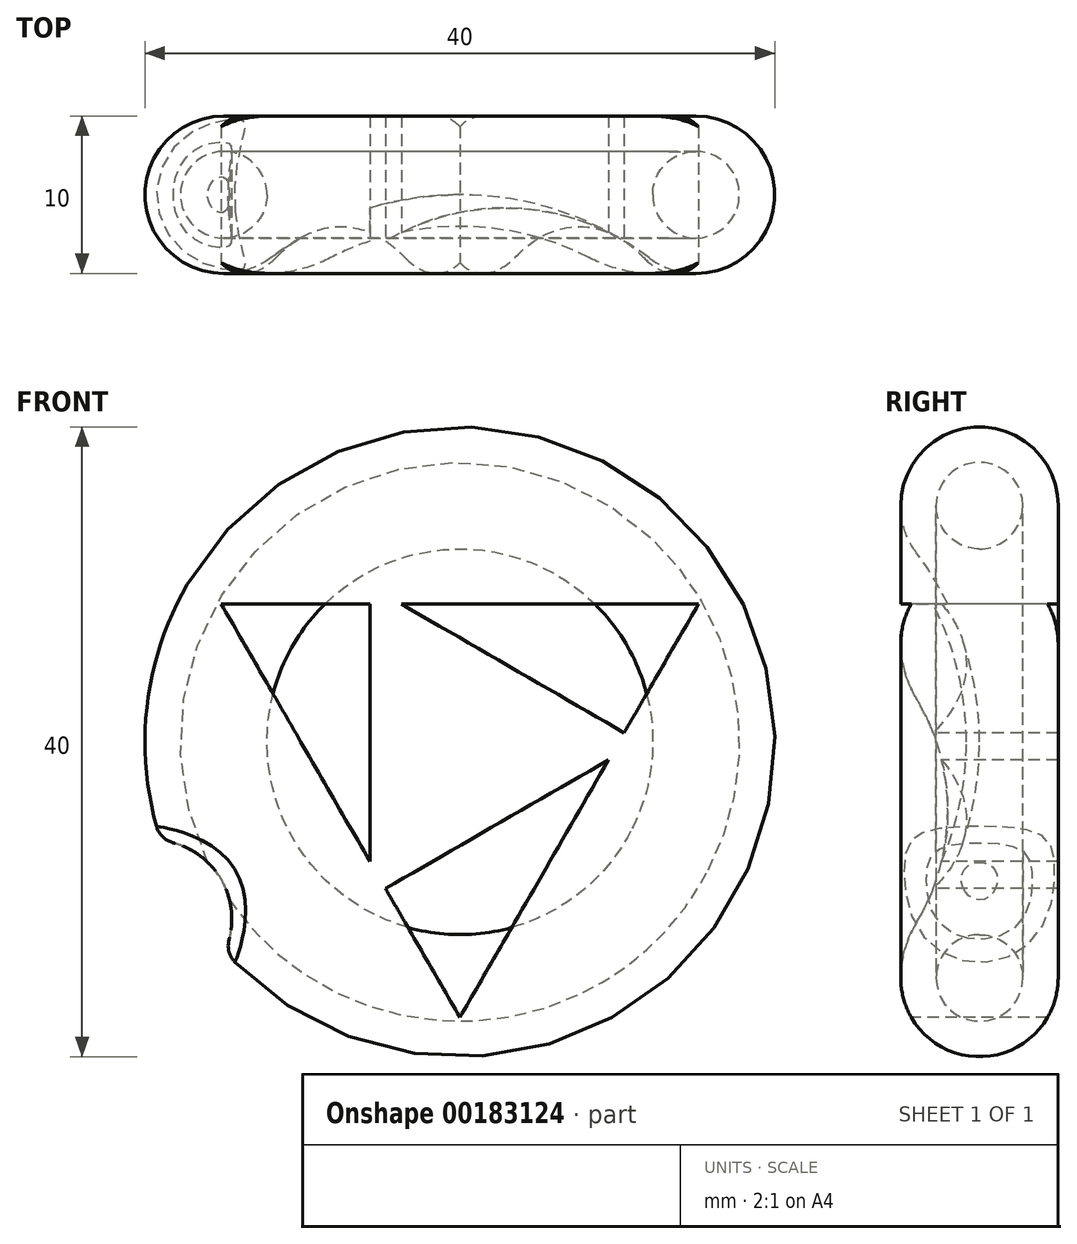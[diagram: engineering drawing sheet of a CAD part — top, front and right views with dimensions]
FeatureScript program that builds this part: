
annotation { "Feature Type Name" : "Feature", "Feature Type Description" : "" }
export const myFeature = defineFeature(function(context is Context, id is Id, definition is map)
    precondition{}
    {
        {
            var Q0;
            Q0=qCreatedBy(makeId("Top.planeOp"),FACE);
            var sketch = newSketch(context, id + "F0", { "sketchPlane" : qUnion([Q0])});
            skLineSegment(sketch, "E0", {"start": v(-15, 0) * mm, "end": v(0, 0) * mm});
            skArc(sketch, "E1.MirrorCS", {"start": v(-12, -9) * mm, "mid": v(-6.32, -6.03) * mm, "end": v(0, -5) * mm});
            skArc(sketch, "E2.MirrorCS", {"start": v(-12, -9) * mm, "mid": v(-19.74, -6.58) * mm, "end": v(-15, 0) * mm});
            skLineSegment(sketch, "E3.MirrorCS", {"start": v(0, 0) * mm, "end": v(0, -5) * mm});
            skSolve(sketch);
        }
        {
            var Q0;
            Q0=makeQuery(id+"F0.imprint","IMPRINT",FACE,{"disambiguationData":[TD([[makeQuery(id+"F0.imprint","IMPRINT",EDGE,{"derivedFrom":sQuery(id+"F0.wireOp",EDGE,"E0")}),-1.0]])]});
            var Q1;
            Q1=sQuery(id+"F0.wireOp",EDGE,"E3.MirrorCS");
            revolve(context, id + "F1", {"entities" : qUnion([Q0]), "axis" : qUnion([Q1]), "revolveType" : RevolveType.FULL});
        }
        {
            var Q0;
            Q0=qCreatedBy(makeId("Front.planeOp"),FACE);
            cPlane(context, id + "F2", {"entities" : qUnion([Q0]), "cplaneType" : CPlaneType.OFFSET, "offset" : 10 * mm, "width" : 150 * mm, "height" : 150 * mm});
        }
        {
            var Q0;
            Q0=qCreatedBy(id+"F2.planeOp",FACE);
            var sketch = newSketch(context, id + "F3", { "sketchPlane" : qUnion([Q0])});
            skPoint(sketch, "E4.center", {"position": v(0, 0) * mm});
            skLineSegment(sketch, "E5", {"start": v(0, -17.5) * mm, "end": v(9.44, -1.15) * mm});
            skLineSegment(sketch, "E6", {"start": v(-4.72, -9.33) * mm, "end": v(0, -17.5) * mm});
            skLineSegment(sketch, "E7", {"start": v(9.44, -1.15) * mm, "end": v(-4.72, -9.33) * mm});
            skLineSegment(sketch, "E8.1.0", {"start": v(-3.72, 8.75) * mm, "end": v(10.44, 0.58) * mm});
            skLineSegment(sketch, "E8.1.1", {"start": v(10.44, 0.58) * mm, "end": v(15.16, 8.75) * mm});
            skLineSegment(sketch, "E8.1.2", {"start": v(15.16, 8.75) * mm, "end": v(-3.72, 8.75) * mm});
            skLineSegment(sketch, "E8.2.0", {"start": v(-5.72, -7.6) * mm, "end": v(-5.72, 8.75) * mm});
            skLineSegment(sketch, "E8.2.1", {"start": v(-5.72, 8.75) * mm, "end": v(-15.16, 8.75) * mm});
            skLineSegment(sketch, "E8.2.2", {"start": v(-15.16, 8.75) * mm, "end": v(-5.72, -7.6) * mm});
            skLineSegment(sketch, "E9", {"start": v(9.44, -1.15) * mm, "end": v(10.44, 0.58) * mm, "construction": true});
            skLineSegment(sketch, "E10", {"start": v(-3.72, 8.75) * mm, "end": v(-5.72, 8.75) * mm, "construction": true});
            skLineSegment(sketch, "E11", {"start": v(-5.72, -7.6) * mm, "end": v(-4.72, -9.33) * mm, "construction": true});
            skPoint(sketch, "E12", {"position": v(-15.16, 8.75) * mm});
            skCircle(sketch, "E13.0", {"center": v(0, 0) * mm, "radius": 15 * mm, "construction": true});
            skLineSegment(sketch, "E14", {"start": v(-17.32, 10) * mm, "end": v(-13, 7.5) * mm, "construction": true});
            skCircle(sketch, "E15", {"center": v(0, 0) * mm, "radius": 20 * mm, "construction": true});
            skSolve(sketch);
        }
        {
            var Q0;
            Q0 = qSketchRegion(id + "F3", true);
            extrude(context, id + "F4", {"entities" : qUnion([Q0]), "operationType" : NewBodyOperationType.REMOVE, "endBound" : BoundingType.THROUGH_ALL, "oppositeDirection" : true, "depth" : 25 * mm});
        }
        {
            var Q0;
            Q0=qCreatedBy(makeId("Top.planeOp"),FACE);
            var sketch = newSketch(context, id + "F5", { "sketchPlane" : qUnion([Q0])});
            skCircle(sketch, "E16", {"center": v(-15, -5) * mm, "radius": 2.75 * mm});
            skSolve(sketch);
        }
        {
            var Q0;
            Q0 = qSketchRegion(id + "F5", true);
            var Q1;
            Q1=sQuery(id+"F0.wireOp",EDGE,"E3.MirrorCS");
            revolve(context, id + "F6", {"entities" : qUnion([Q0]), "axis" : qUnion([Q1]), "revolveType" : RevolveType.FULL});
        }
        {
            var Q0;
            Q0=qCreatedBy(id+"F2.planeOp",FACE);
            var sketch = newSketch(context, id + "F7", { "sketchPlane" : qUnion([Q0])});
            skCircle(sketch, "E17", {"center": v(-19.49, -11.25) * mm, "radius": 5 * mm});
            skPoint(sketch, "E18.center", {"position": v(0, 0) * mm});
            skLineSegment(sketch, "E19.0", {"start": v(-6.47, 21.83) * mm, "end": v(-6.47, 21.83) * mm});
            skCircle(sketch, "E20", {"center": v(0, 0) * mm, "radius": 20 * mm, "construction": true});
            skLineSegment(sketch, "E21", {"start": v(-19.49, -11.25) * mm, "end": v(-17.32, -10) * mm});
            skLineSegment(sketch, "E22", {"start": v(-17.32, -10) * mm, "end": v(-15.16, -8.75) * mm});
            skPoint(sketch, "E23.0", {"position": v(-15.16, 8.75) * mm});
            skPoint(sketch, "E24.0", {"position": v(0, -17.5) * mm});
            skLineSegment(sketch, "E25", {"start": v(-15.16, -8.75) * mm, "end": v(-15.16, 8.75) * mm, "construction": true});
            skLineSegment(sketch, "E26", {"start": v(-15.16, -8.75) * mm, "end": v(0, -17.5) * mm, "construction": true});
            skSolve(sketch);
        }
        {
            var Q0;
            Q0 = qSketchRegion(id + "F7", true);
            extrude(context, id + "F8", {"entities" : qUnion([Q0]), "operationType" : NewBodyOperationType.REMOVE, "endBound" : BoundingType.THROUGH_ALL, "oppositeDirection" : true, "depth" : 25 * mm});
        }
        {
            var Q0;
            Q0=makeQuery(id+"F8.boolean.opBoolean","COPY",FACE,{"disambiguationData":[TD([makeQuery(id+"F1.opRevolve","SWEPT_FACE",FACE,{"disambiguationData":[OSD([sQuery(id+"F0.wireOp",EDGE,"E2.MirrorCS")])]})])],"derivedFrom":makeQuery(id+"F8.opExtrude","SWEPT_FACE",FACE,{"disambiguationData":[OSD([sQuery(id+"F7.wireOp",EDGE,"E17")])]})});
            var Q1;
            Q1=makeQuery(id+"F8.boolean.opBoolean","COPY",FACE,{"disambiguationData":[TD([makeQuery(id+"F1.opRevolve","SWEPT_FACE",FACE,{"disambiguationData":[OSD([sQuery(id+"F0.wireOp",EDGE,"E2.MirrorCS")])]})])],"derivedFrom":makeQuery(id+"F8.opExtrude","SWEPT_FACE",FACE,{"disambiguationData":[OSD([sQuery(id+"F7.wireOp",EDGE,"E18.1.0")])]})});
            var Q2;
            Q2=makeQuery(id+"F8.boolean.opBoolean","COPY",FACE,{"disambiguationData":[TD([makeQuery(id+"F1.opRevolve","SWEPT_FACE",FACE,{"disambiguationData":[OSD([sQuery(id+"F0.wireOp",EDGE,"E2.MirrorCS")])]})])],"derivedFrom":makeQuery(id+"F8.opExtrude","SWEPT_FACE",FACE,{"disambiguationData":[OSD([sQuery(id+"F7.wireOp",EDGE,"E18.2.0")])]})});
            var Q3;
            Q3=makeQuery(id+"F8.boolean.opBoolean","COPY",FACE,{"disambiguationData":[TD([makeQuery(id+"F1.opRevolve","SWEPT_FACE",FACE,{"disambiguationData":[OSD([sQuery(id+"F0.wireOp",EDGE,"E2.MirrorCS")])]})])],"derivedFrom":makeQuery(id+"F8.opExtrude","SWEPT_FACE",FACE,{"disambiguationData":[OSD([sQuery(id+"F7.wireOp",EDGE,"E18.3.0")])]})});
            var Q4;
            Q4=makeQuery(id+"F8.boolean.opBoolean","COPY",FACE,{"disambiguationData":[TD([makeQuery(id+"F1.opRevolve","SWEPT_FACE",FACE,{"disambiguationData":[OSD([sQuery(id+"F0.wireOp",EDGE,"E2.MirrorCS")])]})])],"derivedFrom":makeQuery(id+"F8.opExtrude","SWEPT_FACE",FACE,{"disambiguationData":[OSD([sQuery(id+"F7.wireOp",EDGE,"E18.4.0")])]})});
            var Q5;
            Q5=makeQuery(id+"F8.boolean.opBoolean","COPY",FACE,{"disambiguationData":[TD([makeQuery(id+"F1.opRevolve","SWEPT_FACE",FACE,{"disambiguationData":[OSD([sQuery(id+"F0.wireOp",EDGE,"E2.MirrorCS")])]})])],"derivedFrom":makeQuery(id+"F8.opExtrude","SWEPT_FACE",FACE,{"disambiguationData":[OSD([sQuery(id+"F7.wireOp",EDGE,"E18.5.0")])]})});
            var Q6;
            Q6=makeQuery(id+"F8.boolean.opBoolean","COPY",FACE,{"disambiguationData":[TD([makeQuery(id+"F1.opRevolve","SWEPT_FACE",FACE,{"disambiguationData":[OSD([sQuery(id+"F0.wireOp",EDGE,"E2.MirrorCS")])]})])],"derivedFrom":makeQuery(id+"F8.opExtrude","SWEPT_FACE",FACE,{"disambiguationData":[OSD([sQuery(id+"F7.wireOp",EDGE,"E18.6.0")])]})});
            var Q7;
            Q7=makeQuery(id+"F8.boolean.opBoolean","COPY",FACE,{"disambiguationData":[TD([makeQuery(id+"F1.opRevolve","SWEPT_FACE",FACE,{"disambiguationData":[OSD([sQuery(id+"F0.wireOp",EDGE,"E2.MirrorCS")])]})])],"derivedFrom":makeQuery(id+"F8.opExtrude","SWEPT_FACE",FACE,{"disambiguationData":[OSD([sQuery(id+"F7.wireOp",EDGE,"E18.7.0")])]})});
            var Q8;
            Q8=makeQuery(id+"F8.boolean.opBoolean","COPY",FACE,{"disambiguationData":[TD([makeQuery(id+"F1.opRevolve","SWEPT_FACE",FACE,{"disambiguationData":[OSD([sQuery(id+"F0.wireOp",EDGE,"E2.MirrorCS")])]})])],"derivedFrom":makeQuery(id+"F8.opExtrude","SWEPT_FACE",FACE,{"disambiguationData":[OSD([sQuery(id+"F7.wireOp",EDGE,"E18.8.0")])]})});
            fillet(context, id + "F9", {"entities" : qUnion([Q0, Q1, Q2, Q3, Q4, Q5, Q6, Q7, Q8]), "radius" : 1.5 * mm, "tangentPropagation" : true, "allowEdgeOverflow" : false});
        }
        {
            var Q0;
            Q0=qCreatedBy(makeId("Front.planeOp"),FACE);
            var Q1;
            Q1=qCreatedBy(id+"F2.planeOp",FACE);
            cPlane(context, id + "F10", {"entities" : qUnion([Q0, Q1]), "cplaneType" : CPlaneType.MID_PLANE, "offset" : 25 * mm, "width" : 150 * mm, "height" : 150 * mm});
        }
        {
            var Q0;
            Q0=qCreatedBy(id+"F10.planeOp",FACE);
            var sketch = newSketch(context, id + "F11", { "sketchPlane" : qUnion([Q0])});
            skPoint(sketch, "E27.0", {"position": v(0, 0) * mm});
            skPoint(sketch, "E28.0", {"position": v(-15, 0) * mm});
            skCircle(sketch, "E29", {"center": v(0, 0) * mm, "radius": 15 * mm, "construction": true});
            skSolve(sketch);
        }
    });
